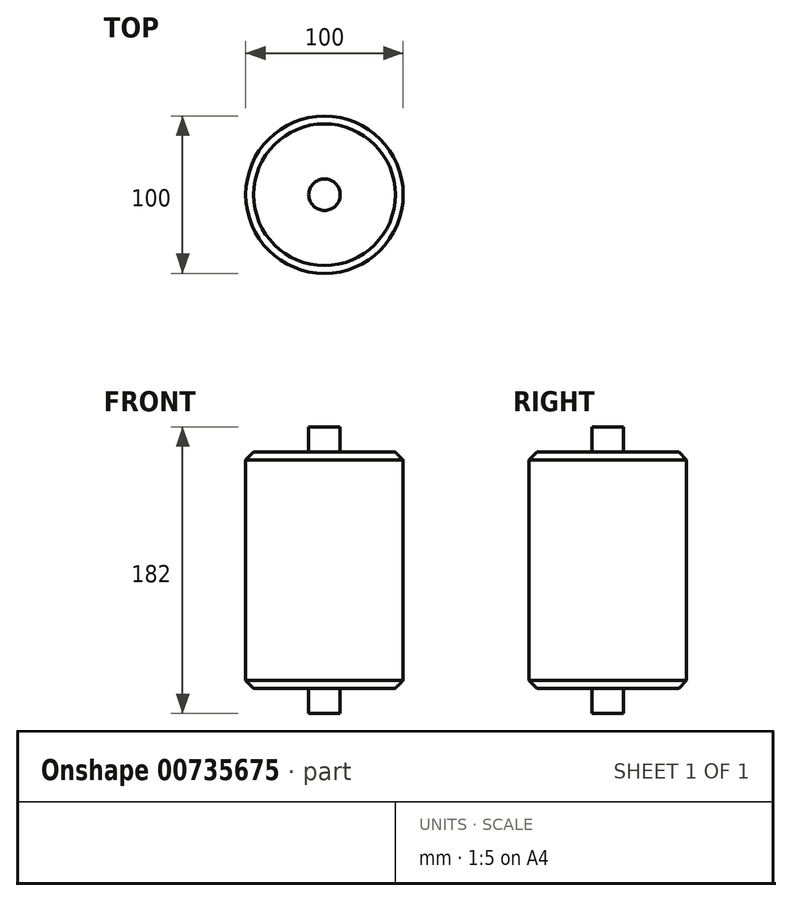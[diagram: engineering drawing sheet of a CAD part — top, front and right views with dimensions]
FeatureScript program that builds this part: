
annotation { "Feature Type Name" : "Feature", "Feature Type Description" : "" }
export const myFeature = defineFeature(function(context is Context, id is Id, definition is map)
    precondition{}
    {
        {
            var Q0;
            Q0=qCreatedBy(makeId("Top.planeOp"),FACE);
            var sketch = newSketch(context, id + "F0", { "sketchPlane" : qUnion([Q0])});
            skCircle(sketch, "E0", {"center": v(0, 0) * mm, "radius": 10 * mm});
            skSolve(sketch);
        }
        {
            var Q0;
            Q0 = qSketchRegion(id + "F0", true);
            extrude(context, id + "F1", {"entities" : qUnion([Q0]), "endBound" : BoundingType.SYMMETRIC, "depth" : 182 * mm, "offsetDistance" : 25 * mm});
        }
        {
            var Q0;
            Q0=qCreatedBy(makeId("Top.planeOp"),FACE);
            var sketch = newSketch(context, id + "F2", { "sketchPlane" : qUnion([Q0])});
            skCircle(sketch, "E1", {"center": v(0, 0) * mm, "radius": 50 * mm});
            skSolve(sketch);
        }
        {
            var Q0;
            Q0 = qSketchRegion(id + "F2", true);
            extrude(context, id + "F3", {"entities" : qUnion([Q0]), "operationType" : NewBodyOperationType.ADD, "endBound" : BoundingType.SYMMETRIC, "depth" : 150 * mm, "offsetDistance" : 25 * mm});
        }
        {
            var Q0;
            Q0=makeQuery(id+"F3.opExtrude","CAP_EDGE",EDGE,{"disambiguationData":[OSD([sQuery(id+"F2.wireOp",EDGE,"E1")])],"isStart":true});
            chamfer(context, id + "F4", {"entities" : qUnion([Q0]), "width" : 5 * mm, "tangentPropagation" : true});
        }
        {
            var Q0;
            Q0=makeQuery(id+"F3.opExtrude","CAP_EDGE",EDGE,{"disambiguationData":[OSD([sQuery(id+"F2.wireOp",EDGE,"E1")])],"isStart":false});
            chamfer(context, id + "F5", {"entities" : qUnion([Q0]), "width" : 5 * mm, "tangentPropagation" : true});
        }
    });
